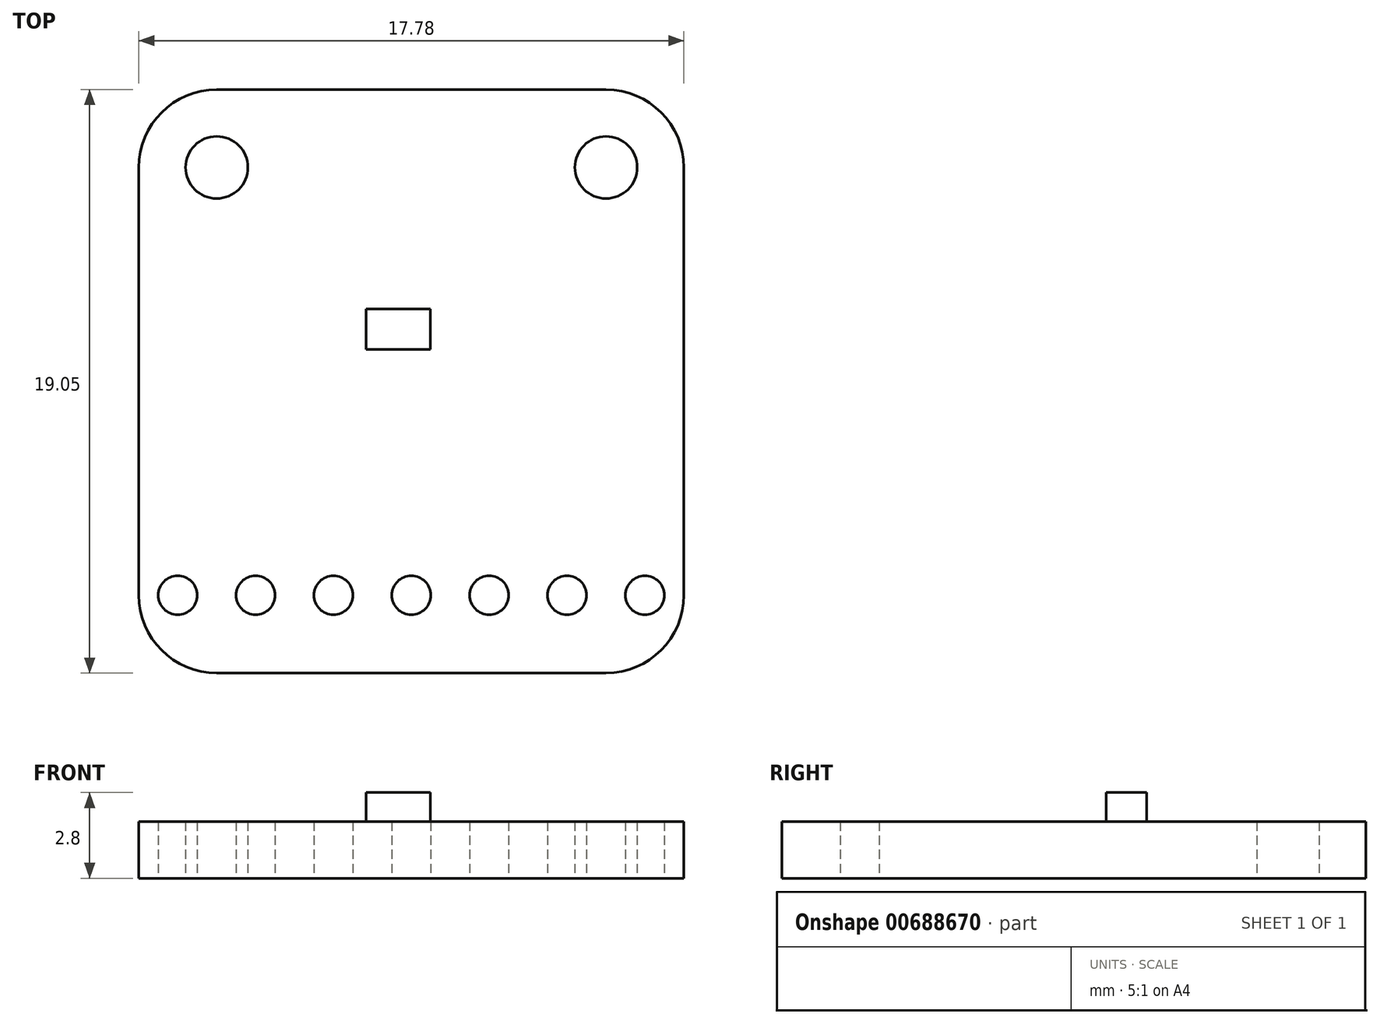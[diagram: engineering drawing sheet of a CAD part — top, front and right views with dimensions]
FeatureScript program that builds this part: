
annotation { "Feature Type Name" : "Feature", "Feature Type Description" : "" }
export const myFeature = defineFeature(function(context is Context, id is Id, definition is map)
    precondition{}
    {
        {
            var Q0;
            Q0=qCreatedBy(makeId("Top.planeOp"),FACE);
            var sketch = newSketch(context, id + "F0", { "sketchPlane" : qUnion([Q0])});
            skLineSegment(sketch, "E0.bottom", {"start": v(0, -16.51) * mm, "end": v(12.7, -16.51) * mm});
            skLineSegment(sketch, "E0.top", {"start": v(0, 2.54) * mm, "end": v(12.7, 2.54) * mm});
            skLineSegment(sketch, "E0.left", {"start": v(-2.54, -13.97) * mm, "end": v(-2.54, 0) * mm});
            skLineSegment(sketch, "E0.right", {"start": v(15.24, -13.97) * mm, "end": v(15.24, 0) * mm});
            skCircle(sketch, "E1", {"center": v(0, 0) * mm, "radius": 1.01 * mm});
            skCircle(sketch, "E2", {"center": v(12.7, 0) * mm, "radius": 1.01 * mm});
            skLineSegment(sketch, "E3", {"start": v(-1.27, -13.97) * mm, "end": v(1.27, -13.97) * mm, "construction": true});
            skLineSegment(sketch, "E4", {"start": v(1.27, -13.97) * mm, "end": v(3.8, -13.97) * mm, "construction": true});
            skLineSegment(sketch, "E5", {"start": v(3.8, -13.97) * mm, "end": v(6.35, -13.97) * mm, "construction": true});
            skLineSegment(sketch, "E6", {"start": v(6.35, -13.97) * mm, "end": v(8.89, -13.97) * mm, "construction": true});
            skLineSegment(sketch, "E7", {"start": v(8.89, -13.97) * mm, "end": v(11.43, -13.97) * mm, "construction": true});
            skLineSegment(sketch, "E8", {"start": v(11.43, -13.97) * mm, "end": v(13.97, -13.97) * mm, "construction": true});
            skCircle(sketch, "E9", {"center": v(-1.27, -13.97) * mm, "radius": 0.64 * mm});
            skCircle(sketch, "E10", {"center": v(1.27, -13.97) * mm, "radius": 0.64 * mm});
            skCircle(sketch, "E11", {"center": v(3.8, -13.97) * mm, "radius": 0.64 * mm});
            skCircle(sketch, "E12", {"center": v(6.35, -13.97) * mm, "radius": 0.64 * mm});
            skCircle(sketch, "E13", {"center": v(8.89, -13.97) * mm, "radius": 0.64 * mm});
            skCircle(sketch, "E14", {"center": v(11.43, -13.97) * mm, "radius": 0.64 * mm});
            skCircle(sketch, "E15", {"center": v(13.97, -13.97) * mm, "radius": 0.64 * mm});
            skPoint(sketch, "E16.visualSharp", {"position": v(-2.54, 2.54) * mm});
            skArc(sketch, "E16.filletArc", {"start": v(0, 2.54) * mm, "mid": v(-1.8, 1.8) * mm, "end": v(-2.54, 0) * mm});
            skPoint(sketch, "E17.visualSharp", {"position": v(15.24, 2.54) * mm});
            skArc(sketch, "E17.filletArc", {"start": v(15.24, 0) * mm, "mid": v(14.5, 1.8) * mm, "end": v(12.7, 2.54) * mm});
            skPoint(sketch, "E18.visualSharp", {"position": v(15.24, -16.51) * mm});
            skArc(sketch, "E18.filletArc", {"start": v(12.7, -16.51) * mm, "mid": v(14.5, -15.77) * mm, "end": v(15.24, -13.97) * mm});
            skPoint(sketch, "E19.visualSharp", {"position": v(-2.54, -16.51) * mm});
            skArc(sketch, "E19.filletArc", {"start": v(-2.54, -13.97) * mm, "mid": v(-1.8, -15.77) * mm, "end": v(0, -16.51) * mm});
            skLineSegment(sketch, "E20", {"start": v(0, 0) * mm, "end": v(12.7, 0) * mm, "construction": true});
            skLineSegment(sketch, "E21", {"start": v(6.35, 0) * mm, "end": v(6.35, -13.97) * mm, "construction": true});
            skSolve(sketch);
        }
        {
            var Q0;
            Q0 = qSketchRegion(id + "F0", true);
            extrude(context, id + "F1", {"entities" : qUnion([Q0]), "depth" : 1.85 * mm, "offsetDistance" : 25 * mm});
        }
        {
            var Q0;
            Q0=makeQuery(id+"F1.opExtrude","CAP_FACE",FACE,{"disambiguationData":[OSD([sQuery(id+"F0.wireOp",EDGE,"E0.bottom"),sQuery(id+"F0.wireOp",EDGE,"E0.top"),sQuery(id+"F0.wireOp",EDGE,"E0.left"),sQuery(id+"F0.wireOp",EDGE,"E0.right"),sQuery(id+"F0.wireOp",EDGE,"E1"),sQuery(id+"F0.wireOp",EDGE,"E2"),sQuery(id+"F0.wireOp",EDGE,"E9"),sQuery(id+"F0.wireOp",EDGE,"E10"),sQuery(id+"F0.wireOp",EDGE,"E11"),sQuery(id+"F0.wireOp",EDGE,"E12"),sQuery(id+"F0.wireOp",EDGE,"E13"),sQuery(id+"F0.wireOp",EDGE,"E14"),sQuery(id+"F0.wireOp",EDGE,"E15"),sQuery(id+"F0.wireOp",EDGE,"E16.filletArc"),sQuery(id+"F0.wireOp",EDGE,"E17.filletArc"),sQuery(id+"F0.wireOp",EDGE,"E18.filletArc"),sQuery(id+"F0.wireOp",EDGE,"E19.filletArc")])],"isStart":false});
            var sketch = newSketch(context, id + "F2", { "sketchPlane" : qUnion([Q0])});
            skLineSegment(sketch, "E22.bottom", {"start": v(4.87, -4.62) * mm, "end": v(6.96, -4.62) * mm});
            skLineSegment(sketch, "E22.top", {"start": v(4.87, -5.94) * mm, "end": v(6.96, -5.94) * mm});
            skLineSegment(sketch, "E22.left", {"start": v(4.87, -4.62) * mm, "end": v(4.87, -5.94) * mm});
            skLineSegment(sketch, "E22.right", {"start": v(6.96, -4.62) * mm, "end": v(6.96, -5.94) * mm});
            skSolve(sketch);
        }
        {
            var Q0;
            Q0 = qSketchRegion(id + "F2", true);
            extrude(context, id + "F3", {"entities" : qUnion([Q0]), "operationType" : NewBodyOperationType.ADD, "depth" : 0.95 * mm, "offsetDistance" : 25 * mm});
        }
    });
